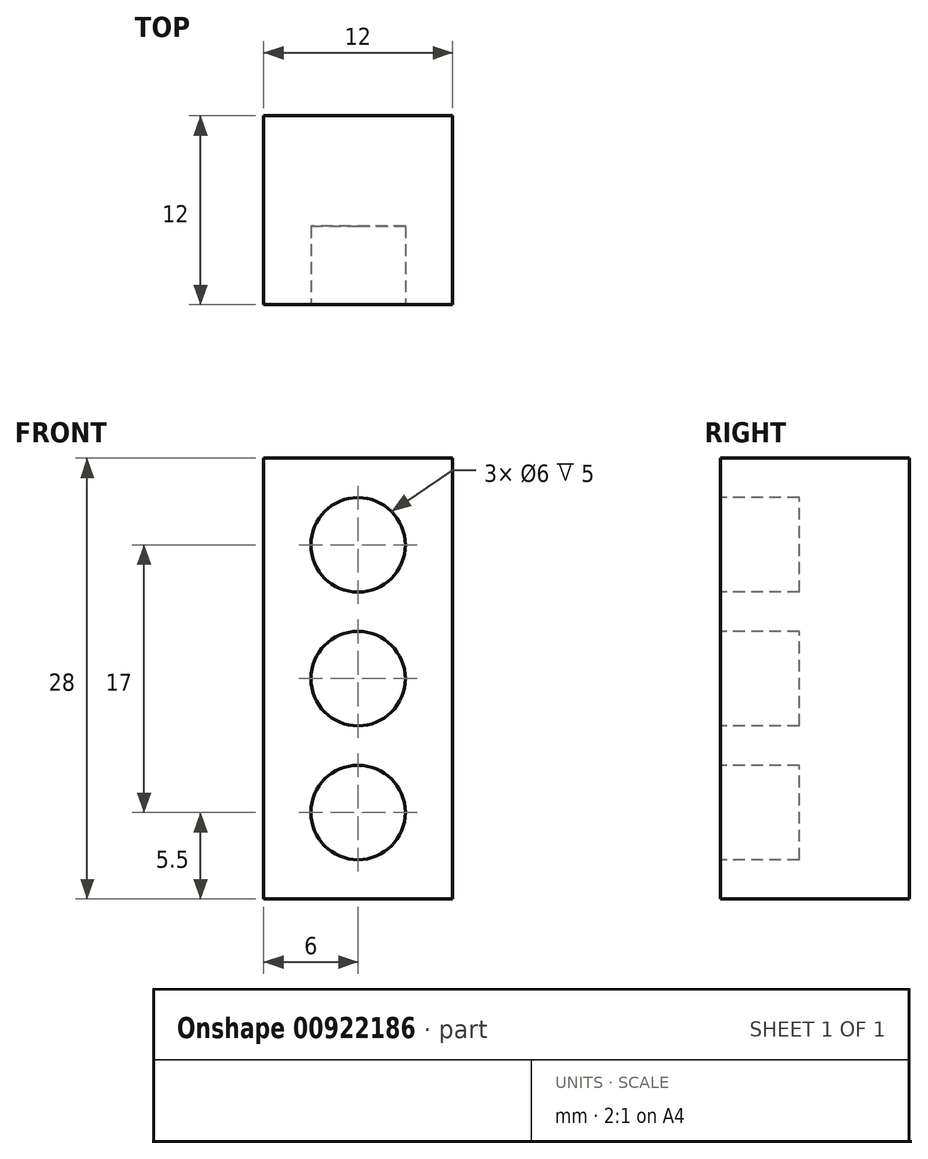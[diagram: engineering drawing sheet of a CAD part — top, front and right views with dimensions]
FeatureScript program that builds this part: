
annotation { "Feature Type Name" : "Feature", "Feature Type Description" : "" }
export const myFeature = defineFeature(function(context is Context, id is Id, definition is map)
    precondition{}
    {
        {
            var Q0;
            Q0=qCreatedBy(makeId("Front.planeOp"),FACE);
            var sketch = newSketch(context, id + "F0", { "sketchPlane" : qUnion([Q0])});
            skLineSegment(sketch, "E0.bottom", {"start": v(6, -14) * mm, "end": v(-6, -14) * mm});
            skLineSegment(sketch, "E0.top", {"start": v(6, 14) * mm, "end": v(-6, 14) * mm});
            skLineSegment(sketch, "E0.left", {"start": v(6, -14) * mm, "end": v(6, 14) * mm});
            skLineSegment(sketch, "E0.right", {"start": v(-6, -14) * mm, "end": v(-6, 14) * mm});
            skPoint(sketch, "E0.middle", {"position": v(0, 0) * mm});
            skSolve(sketch);
        }
        {
            var Q0;
            Q0=makeQuery(id+"F0.imprint","IMPRINT",FACE,{"disambiguationData":[TD([[makeQuery(id+"F0.imprint","IMPRINT",EDGE,{"derivedFrom":sQuery(id+"F0.wireOp",EDGE,"E0.bottom")}),-1.0]])]});
            extrude(context, id + "F1", {"entities" : qUnion([Q0]), "depth" : 12 * mm, "offsetDistance" : 25 * mm});
        }
        {
            var Q0;
            Q0=makeQuery(id+"F1.opExtrude","CAP_FACE",FACE,{"disambiguationData":[OSD([sQuery(id+"F0.wireOp",EDGE,"E0.bottom"),sQuery(id+"F0.wireOp",EDGE,"E0.top"),sQuery(id+"F0.wireOp",EDGE,"E0.left"),sQuery(id+"F0.wireOp",EDGE,"E0.right")])],"isStart":false});
            var sketch = newSketch(context, id + "F2", { "sketchPlane" : qUnion([Q0])});
            skCircle(sketch, "E1", {"center": v(0, 8.5) * mm, "radius": 3 * mm});
            skCircle(sketch, "E2", {"center": v(0, 0) * mm, "radius": 3 * mm});
            skCircle(sketch, "E3", {"center": v(0, -8.5) * mm, "radius": 3 * mm});
            skSolve(sketch);
        }
        {
            var Q0;
            Q0=makeQuery(id+"F2.imprint","IMPRINT",FACE,{"disambiguationData":[TD([[makeQuery(id+"F2.imprint","IMPRINT",EDGE,{"derivedFrom":sQuery(id+"F2.wireOp",EDGE,"E1")}),1.0]])]});
            var Q1;
            Q1=makeQuery(id+"F2.imprint","IMPRINT",FACE,{"disambiguationData":[TD([[makeQuery(id+"F2.imprint","IMPRINT",EDGE,{"derivedFrom":sQuery(id+"F2.wireOp",EDGE,"E2")}),1.0]])]});
            var Q2;
            Q2=makeQuery(id+"F2.imprint","IMPRINT",FACE,{"disambiguationData":[TD([[makeQuery(id+"F2.imprint","IMPRINT",EDGE,{"derivedFrom":sQuery(id+"F2.wireOp",EDGE,"E3")}),1.0]])]});
            extrude(context, id + "F3", {"entities" : qUnion([Q0, Q1, Q2]), "operationType" : NewBodyOperationType.REMOVE, "oppositeDirection" : true, "depth" : 5 * mm, "offsetDistance" : 25 * mm});
        }
    });
